# Revit family: BuzziShade
name_source: partatom
category: Lighting Fixtures
revit_build: Autodesk Revit 2018 (Build: 20190510_1515(x64)
units: mm (PartAtom-declared; Revit-internal decimal feet)

## family parameters
Always vertical = Yes
Cut with Voids When Loaded = No
Host = Ceiling
Light Source = Yes
OmniClass Number = 23.80.70.11
OmniClass Title = Luminaries for Internal Lighting
Part Type = Normal
Room Calculation Point = No
Round Connector Dimension = Use Diameter
Shared = No

## types (12) — shared parameters
Cables = <By Category>
Color Filter = 16777215
Dimming Lamp Color Temperature Shift = <None>
Fixture Height AFF = 183 cm
Frame = <By Category>
Housing = <By Category>
Lens = <By Category>
Light Source Symbol Size = 61 cm
Shade = <By Category>
Stitch = <By Category>

## per-type parameters (varying)
| type | L | L Cables | L Shade Type | M | M Cables | M Shade Type | Medium or Large Light Source | XL | XL Shade Type | XXL | XXL Type |
| XL- LED Disk | No | No | L Shade : L shade with no light source | No | No | M Shade : M shade with spotlight | No | Yes | XL Shade | No | XXL Shade |
| XL- No Light Source | No | No | L Shade : L shade with no light source | No | No | M Shade : M shade with spotlight | No | Yes | XL Shade : XL Shade without Light Source | No | XXL Shade |
| XXL- LED Disk | No | No | L Shade : L shade with no light source | No | No | M Shade : M shade with spotlight | No | No | XL Shade : XL Shade without Light Source | Yes | XXL Shade |
| XXL- No Light Source | No | No | L Shade : L shade with no light source | No | No | M Shade : M shade with spotlight | No | No | XL Shade : XL Shade without Light Source | Yes | XXL Shade : XXL without Light Source |
| Large- No Light Source | Yes | Yes | L Shade : L shade with no light source | No | No | M Shade : M shade with spotlight | No | No | XL Shade : XL Shade without Light Source | No | XXL Shade : XXL without Light Source |
| Large- LED Globe | Yes | Yes | L Shade : L Shade with Globe | No | No | M Shade : M shade with spotlight | Yes | No | XL Shade : XL Shade without Light Source | No | XXL Shade : XXL without Light Source |
| Large- LED Spot | Yes | Yes | L Shade : L shade with spotlight | No | No | M Shade : M shade with spotlight | Yes | No | XL Shade : XL Shade without Light Source | No | XXL Shade : XXL without Light Source |
| Medium- LED Globe | No | No | L Shade : L shade with no light source | Yes | Yes | M Shade : M Shade with Globe | Yes | No | XL Shade : XL Shade without Light Source | No | XXL Shade : XXL without Light Source |
| Medium- LED Spot | No | No | L Shade : L shade with no light source | Yes | Yes | M Shade : M shade with spotlight | Yes | No | XL Shade : XL Shade without Light Source | No | XXL Shade : XXL without Light Source |
| Medium- No Light Source | No | No | L Shade : L shade with no light source | Yes | Yes | M Shade : M shade with no light source | No | No | XL Shade : XL Shade without Light Source | No | XXL Shade : XXL without Light Source |
| Large- Retrofit | Yes | Yes | L Shade : L Retrofit | No | No | M Shade : M shade with spotlight | No | No | XL Shade : XL Shade without Light Source | No | XXL Shade : XXL without Light Source |
| Medium- Retrofit | No | No | M Shade : M Retrofit | Yes | Yes | M Shade : M shade with spotlight | No | No | XL Shade : XL Shade without Light Source | No | XXL Shade : XXL without Light Source |

## geometry (parser evidence)
native form markers: Sweep x11
no freeform markers — native parametric forms only
